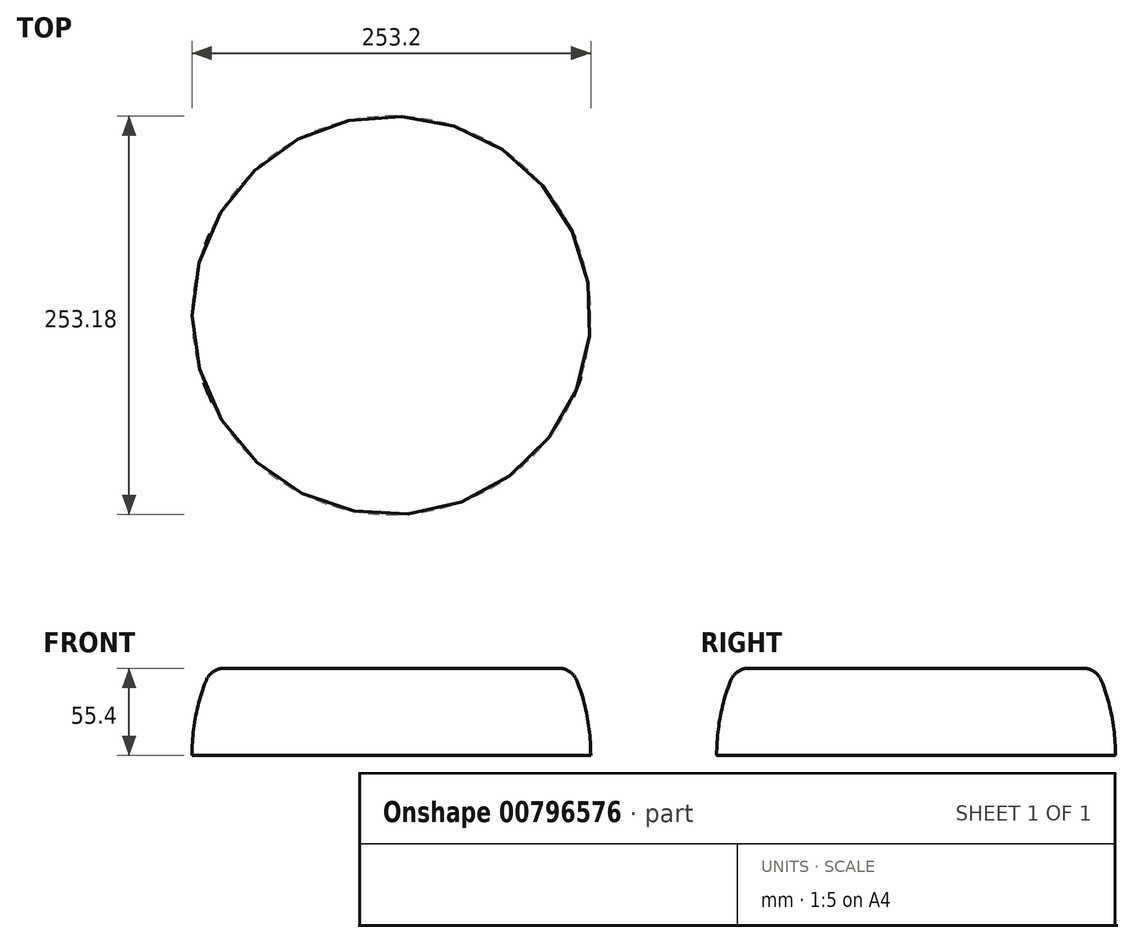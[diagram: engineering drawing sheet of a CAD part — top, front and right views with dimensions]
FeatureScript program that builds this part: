
annotation { "Feature Type Name" : "Feature", "Feature Type Description" : "" }
export const myFeature = defineFeature(function(context is Context, id is Id, definition is map)
    precondition{}
    {
        {
            var Q0;
            Q0=qCreatedBy(makeId("Front.planeOp"),FACE);
            var sketch = newSketch(context, id + "F0", { "sketchPlane" : qUnion([Q0])});
            skArc(sketch, "E0", {"start": v(126.6, 0) * mm, "mid": v(-0.4, 127.93) * mm, "end": v(-127.4, 0) * mm});
            skLineSegment(sketch, "E1", {"start": v(-127.4, 0) * mm, "end": v(126.6, 0) * mm});
            skLineSegment(sketch, "E2", {"start": v(0, 0) * mm, "end": v(0, 127.93) * mm});
            skSolve(sketch);
        }
        {
            var Q0;
            {var subQ3=sQuery(id+"F0.wireOp",EDGE,"E2");Q0=makeQuery(id+"F0.imprint","IMPRINT",FACE,{"disambiguationData":[TD([[makeQuery(id+"F0.imprint","IMPRINT",EDGE,{"derivedFrom":subQ3}),-1.0]])]});}
            var Q1;
            Q1=sQuery(id+"F0.wireOp",EDGE,"E2");
            revolve(context, id + "F1", {"surfaceOperationType" : NewSurfaceOperationType.NEW, "entities" : qUnion([Q0]), "axis" : qUnion([Q1]), "revolveType" : RevolveType.FULL});
        }
        {
            var Q0;
            Q0=qCreatedBy(makeId("Front.planeOp"),FACE);
            var sketch = newSketch(context, id + "F2", { "sketchPlane" : qUnion([Q0])});
            skLineSegment(sketch, "E3.bottom", {"start": v(-126.92, 55.4) * mm, "end": v(132.29, 55.4) * mm});
            skLineSegment(sketch, "E3.top", {"start": v(-126.92, 134) * mm, "end": v(132.29, 134) * mm});
            skLineSegment(sketch, "E3.left", {"start": v(-126.92, 55.4) * mm, "end": v(-126.92, 134) * mm});
            skLineSegment(sketch, "E3.right", {"start": v(132.29, 55.4) * mm, "end": v(132.29, 134) * mm});
            skSolve(sketch);
        }
        {
            var Q0;
            Q0 = qSketchRegion(id + "F2", true);
            extrude(context, id + "F3", {"entities" : qUnion([Q0]), "operationType" : NewBodyOperationType.REMOVE, "endBound" : BoundingType.SYMMETRIC, "depth" : 285 * mm, "offsetDistance" : 25.4 * mm});
        }
        {
            var Q0;
            Q0=makeQuery(id+"F3.boolean.opBoolean","INTERSECT",EDGE,{"derivedFrom":[makeQuery(id+"F1.opRevolve","SWEPT_FACE",FACE,{"disambiguationData":[OSD([sQuery(id+"F0.wireOp",EDGE,"E0")])]}),makeQuery(id+"F3.opExtrude","SWEPT_FACE",FACE,{"disambiguationData":[OSD([sQuery(id+"F2.wireOp",EDGE,"E3.bottom")])]})]});
            fillet(context, id + "F4", {"entities" : qUnion([Q0]), "radius" : 12.7 * mm, "tangentPropagation" : true, "allowEdgeOverflow" : false});
        }
    });
